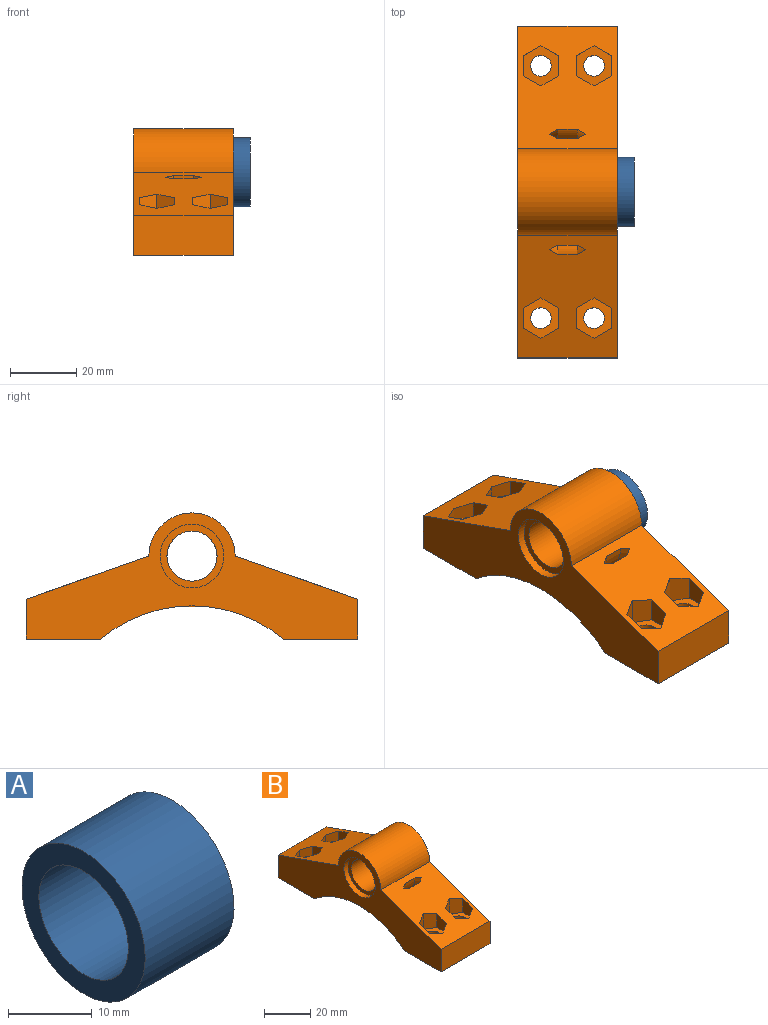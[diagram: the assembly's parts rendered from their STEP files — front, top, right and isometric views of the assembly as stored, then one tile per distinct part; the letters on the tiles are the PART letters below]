
ASSEMBLY  parts=2 mates=1
PART A: 4 faces, bbox 15x20.8x20.8 mm
  f0: cylinder r=7.55mm len=15.1mm, axis (-1,0,0), area 711.6mm2, adj f1,f3
  f1: plane 20.8x20.8mm, normal (-1,0,0), area 160.7mm2, adj f0,f2
  f2: cylinder r=10.4mm len=20.8mm, axis (-1,0,0), area 980.2mm2, adj f1,f3
  f3: plane 20.8x20.8mm, normal (1,0,0), area 160.7mm2, adj f0,f2
PART B: 59 faces, bbox 30x100x38 mm
  f0: cylinder r=7.55mm len=17.5mm, axis (-1,0,0), area 830.2mm2, adj f16,f58
  f1: cylinder r=3.1mm len=10mm, axis (0,0,-1), area 194.8mm2, adj f8,f50
  f2: cylinder r=3.1mm len=10mm, axis (0,0,-1), area 194.8mm2, adj f8,f43
  f3: plane 37x30mm, normal (0,-0.33,0.94), area 948.6mm2, adj f7,f11,f12,f13,f17,f18,f19,f20
  f4: cylinder r=3.1mm len=10mm, axis (0,0,-1), area 194.8mm2, adj f6,f42
  f5: cylinder r=3.1mm len=10mm, axis (0,0,-1), area 194.8mm2, adj f6,f35
  f6: plane 30x22.5mm, normal (0,0,-1), area 614.6mm2, adj f4,f5,f7,f12,f13,f14
  f7: plane 30x12mm, normal (0,-1,0), area 360mm2, adj f3,f6,f12,f13
  f8: plane 30x22.5mm, normal (0,0,-1), area 614.6mm2, adj f1,f2,f9,f12,f13,f14
  f9: plane 30x12mm, normal (0,1,0), area 360mm2, adj f8,f10,f12,f13
  f10: plane 37x30mm, normal (0,0.33,0.94), area 948.6mm2, adj f9,f11,f12,f13,f23,f24,f25,f26
  f11: cylinder r=13mm len=30mm, axis (-1,0,0), area 1225.2mm2, adj f3,f10,f12,f13
  f12: plane 100x38mm, normal (1,0,0), area 1558.6mm2, adj f3,f6,f7,f8,f9,f10,f11,f14
  f13: plane 100x38mm, normal (-1,0,0), area 1618.7mm2, adj f3,f6,f7,f8,f9,f10,f11,f14
  f14: cylinder r=42.81mm len=55mm, axis (-1,0,0), area 1706mm2, adj f6,f8,f12,f13,f17,f18,f19,f20
  f15: cylinder r=10.55mm len=21.1mm, axis (1,0,0), area 662.9mm2, adj f12,f16
  f16: plane 21.1x21.1mm, normal (1,0,0), area 170.6mm2, adj f0,f15
  f17: revolved ~15.72x12.52mm, area 53.4mm2, adj f3,f14,f18,f22
  f18: cylinder r=16.05mm len=14.22mm, axis (1,0,0), area 115mm2, adj f3,f14,f17,f19
  f19: revolved ~15.72x12.52mm, area 53.4mm2, adj f3,f14,f18,f20
  f20: revolved ~15.61x11.12mm, area 50.9mm2, adj f3,f14,f19,f21
  f21: cylinder r=18.96mm len=14.11mm, axis (1,0,0), area 103.8mm2, adj f3,f14,f20,f22
  f22: revolved ~15.61x11.12mm, area 50.9mm2, adj f3,f14,f17,f21
  f23: revolved ~15.53x11.19mm, area 50.9mm2, adj f10,f14,f24,f28
  f24: cylinder r=18.96mm len=14.11mm, axis (1,0,0), area 103.8mm2, adj f10,f14,f23,f25
  f25: revolved ~15.53x11.19mm, area 50.9mm2, adj f10,f14,f24,f26
  f26: revolved ~15.78x12.58mm, area 53.4mm2, adj f10,f14,f25,f27
  f27: cylinder r=16.05mm len=14.22mm, axis (1,0,0), area 115mm2, adj f10,f14,f26,f28
  f28: revolved ~15.78x12.58mm, area 53.4mm2, adj f10,f14,f23,f27
  f29: plane 8.35x5.25mm, normal (-0.5,-0.87,0), area 47.4mm2, adj f3,f30,f34,f35
  f30: plane 8.35x5.25mm, normal (0.5,-0.87,0), area 47.4mm2, adj f3,f29,f31,f35
  f31: plane 7.28x6.06mm, normal (1,0,0), area 37.7mm2, adj f3,f30,f32,f35
  f32: plane 5.25x5.15mm, normal (0.5,0.87,0), area 28mm2, adj f3,f31,f33,f35
  f33: plane 5.25x5.15mm, normal (-0.5,0.87,0), area 28mm2, adj f3,f32,f34,f35
  f34: plane 7.28x6.06mm, normal (-1,0,0), area 37.7mm2, adj f3,f29,f33,f35
  f35: plane 12.12x10.5mm, normal (0,0,1), area 65.3mm2, adj f5,f29,f30,f31,f32,f33,f34
  f36: plane 8.35x5.25mm, normal (0.5,-0.87,0), area 47.4mm2, adj f3,f37,f41,f42
  f37: plane 7.28x6.06mm, normal (1,0,0), area 37.7mm2, adj f3,f36,f38,f42
  f38: plane 5.25x5.15mm, normal (0.5,0.87,0), area 28mm2, adj f3,f37,f39,f42
  f39: plane 5.25x5.15mm, normal (-0.5,0.87,0), area 28mm2, adj f3,f38,f40,f42
  f40: plane 7.28x6.06mm, normal (-1,0,0), area 37.7mm2, adj f3,f39,f41,f42
  f41: plane 8.35x5.25mm, normal (-0.5,-0.87,0), area 47.4mm2, adj f3,f36,f40,f42
  f42: plane 12.12x10.5mm, normal (0,0,1), area 65.3mm2, adj f4,f36,f37,f38,f39,f40,f41
  f43: plane 12.12x10.5mm, normal (0,0,1), area 65.3mm2, adj f2,f44,f45,f46,f47,f48,f49
  f44: plane 8.35x5.25mm, normal (-0.5,0.87,0), area 47.4mm2, adj f10,f43,f45,f49
  f45: plane 7.28x6.06mm, normal (-1,0,0), area 37.7mm2, adj f10,f43,f44,f46
  f46: plane 5.25x5.15mm, normal (-0.5,-0.87,0), area 28mm2, adj f10,f43,f45,f47
  f47: plane 5.25x5.15mm, normal (0.5,-0.87,0), area 28mm2, adj f10,f43,f46,f48
  f48: plane 7.28x6.06mm, normal (1,0,0), area 37.7mm2, adj f10,f43,f47,f49
  f49: plane 8.35x5.25mm, normal (0.5,0.87,0), area 47.4mm2, adj f10,f43,f44,f48
  f50: plane 12.12x10.5mm, normal (0,0,1), area 65.3mm2, adj f1,f51,f52,f53,f54,f55,f56
  f51: plane 8.35x5.25mm, normal (0.5,0.87,0), area 47.4mm2, adj f10,f50,f52,f56
  f52: plane 8.35x5.25mm, normal (-0.5,0.87,0), area 47.4mm2, adj f10,f50,f51,f53
  f53: plane 7.28x6.06mm, normal (-1,0,0), area 37.7mm2, adj f10,f50,f52,f54
  f54: plane 5.25x5.15mm, normal (-0.5,-0.87,0), area 28mm2, adj f10,f50,f53,f55
  f55: plane 5.25x5.15mm, normal (0.5,-0.87,0), area 28mm2, adj f10,f50,f54,f56
  f56: plane 7.28x6.06mm, normal (1,0,0), area 37.7mm2, adj f10,f50,f51,f55
  f57: cylinder r=9.6mm len=19.2mm, axis (-1,0,0), area 150.8mm2, adj f13,f58
  f58: plane 19.2x19.2mm, normal (-1,0,0), area 110.5mm2, adj f0,f57
PLACE A t=(5.21,8.99,19.12)mm
PLACE B t=(0.09,8.99,-5.88)mm fixed
MATE slider A.f0 <-> B.f0  axis (-1,0,0) through (5.21,8.99,19.12)mm
